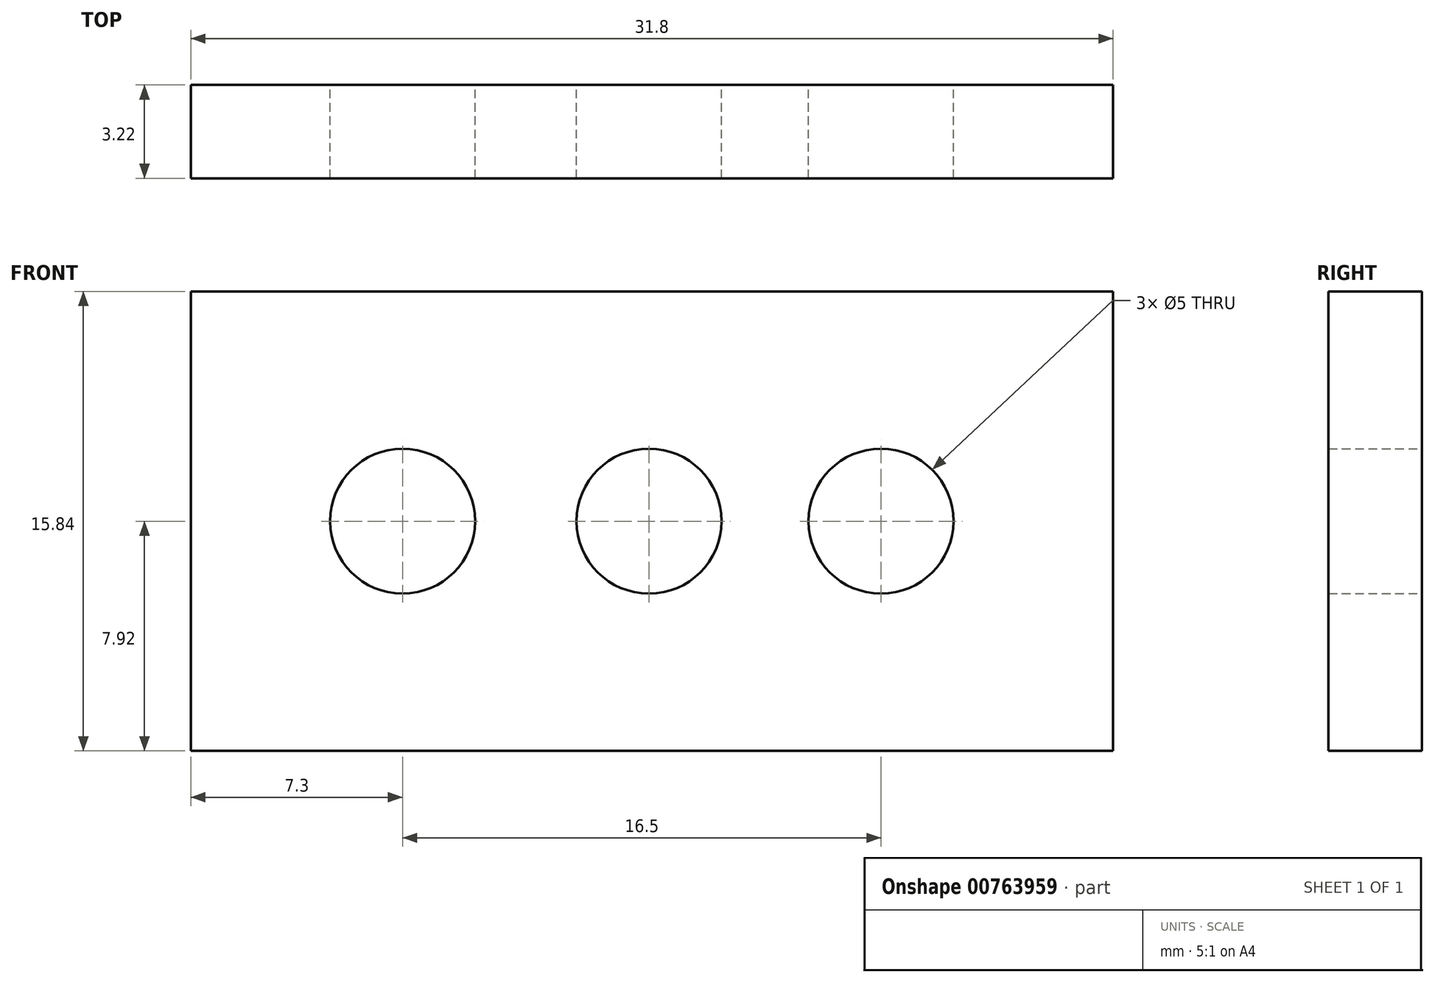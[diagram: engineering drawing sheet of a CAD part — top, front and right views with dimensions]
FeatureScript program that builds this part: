
annotation { "Feature Type Name" : "Feature", "Feature Type Description" : "" }
export const myFeature = defineFeature(function(context is Context, id is Id, definition is map)
    precondition{}
    {
        {
            var Q0;
            Q0=qCreatedBy(makeId("Front.planeOp"),FACE);
            var sketch = newSketch(context, id + "F0", { "sketchPlane" : qUnion([Q0])});
            skLineSegment(sketch, "E0.bottom", {"start": v(-15.9, -7.91) * mm, "end": v(15.9, -7.91) * mm});
            skLineSegment(sketch, "E0.top", {"start": v(-15.9, 7.91) * mm, "end": v(15.9, 7.91) * mm});
            skLineSegment(sketch, "E0.left", {"start": v(-15.9, -7.91) * mm, "end": v(-15.9, 7.91) * mm});
            skLineSegment(sketch, "E0.right", {"start": v(15.9, -7.91) * mm, "end": v(15.9, 7.91) * mm});
            skPoint(sketch, "E0.middle", {"position": v(0, 0) * mm});
            skCircle(sketch, "E1", {"center": v(7.9, 0) * mm, "radius": 2.5 * mm});
            skPoint(sketch, "E1.centerSnap0", {"position": v(15.9, 0) * mm});
            skCircle(sketch, "E2", {"center": v(-0.1, 0) * mm, "radius": 2.5 * mm});
            skCircle(sketch, "E3", {"center": v(-8.6, 0) * mm, "radius": 2.5 * mm});
            skSolve(sketch);
        }
        {
            var Q0;
            Q0 = qSketchRegion(id + "F0", true);
            extrude(context, id + "F1", {"entities" : qUnion([Q0]), "depth" : 3.22 * mm, "offsetDistance" : 25 * mm});
        }
    });
